# Revit family: 01851-B
name_source: partatom
category: Instalační zařizovací předměty
revit_build: Autodesk Revit 2016 (Build: 20161004_0715(x64)
units: mm (PartAtom-declared; Revit-internal decimal feet)

## family parameters
Bod výpočtu místnosti = Ne
Kóta kulaté spojky = Použít průměr
Nadpis OmniClass = Sanitary Equipment
Ořezat dutým tvarem při načtení = Ne
Sdílené = Ne
Typ součásti = Normální
Vždy vertikální = Ano
Založené na pracovní rovině = Ne
Číslo OmniClass = 23.45.05.00

## types (1)
- 01851-B
    Air speed = 305.00 kg/m²
    Air temperature [°C] = 40 °C
    Article number = 01851.B
    DEPTH = 152 mm  [stored 0.498688 ft]
    Electric class = I
    HEIGHT = 323 mm  [stored 1.05971 ft]
    IP code = IPX1
    MATERIAL = <Podle kategorie>
    Noise level = 72
    Power input = 800 W
    Power supply = 0 V
    Product URL link = http://www.nofer.co.uk
    Připojení CW = Ne
    Připojení HW = Ne
    Připojení odpadu = Ne
    Připojení ventilace = Ne
    Surface finish = Polish
    Utility frequency = 0
    Výrobce = Nofer
    WEIGHT = 4.90 kg
    WIDTH = 253 mm  [stored 0.830052 ft]
    Warranty = 2

note: [stored X ft] marks values corroborated as IEEE doubles in the binary element streams (Revit-internal decimal feet)
